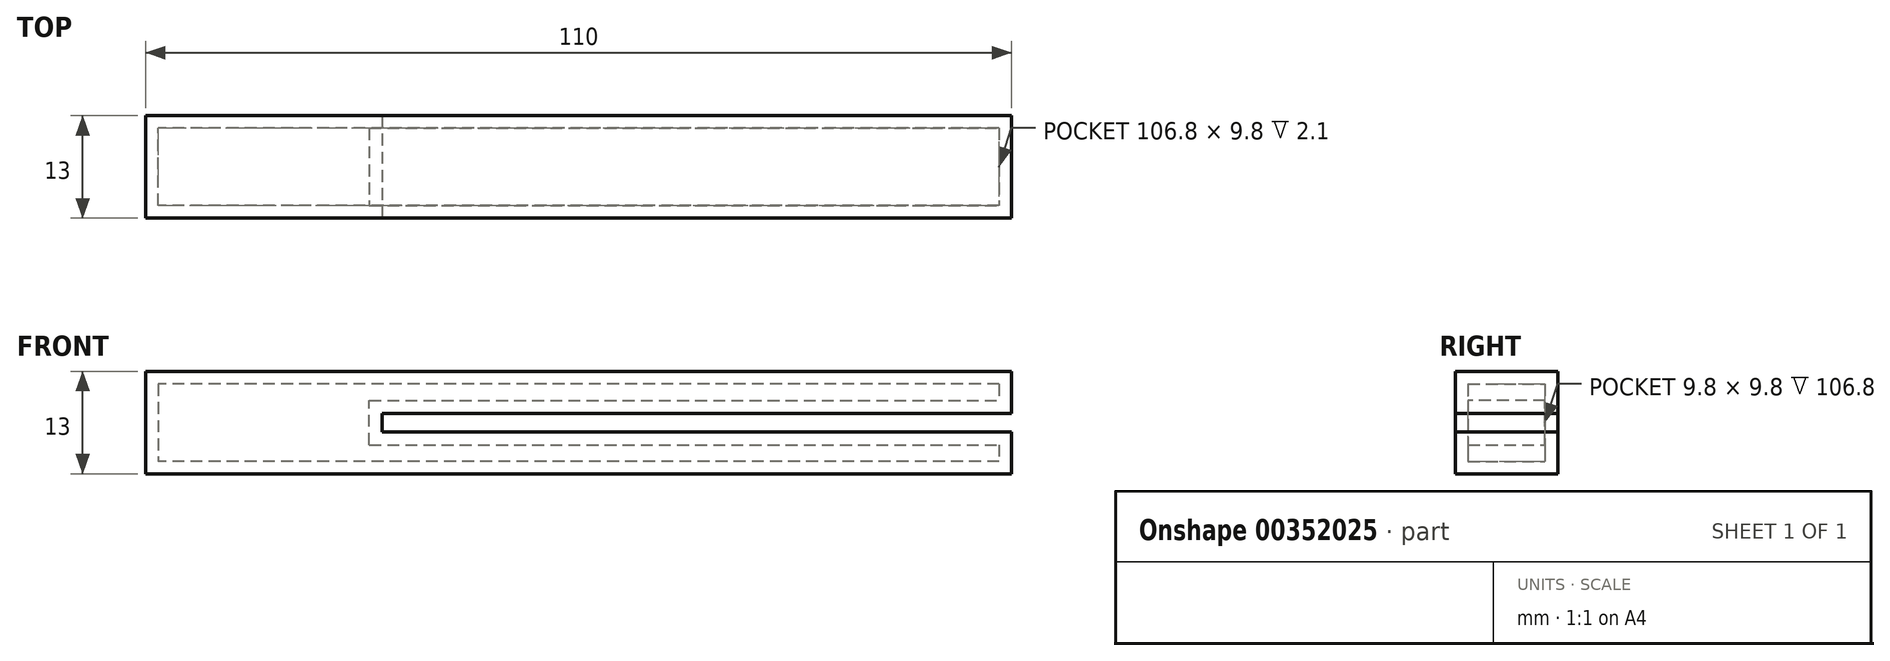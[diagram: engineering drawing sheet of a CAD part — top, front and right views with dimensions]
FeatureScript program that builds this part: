
annotation { "Feature Type Name" : "Feature", "Feature Type Description" : "" }
export const myFeature = defineFeature(function(context is Context, id is Id, definition is map)
    precondition{}
    {
        {
            var Q0;
            Q0=qCreatedBy(makeId("Right.planeOp"),FACE);
            var sketch = newSketch(context, id + "F0", { "sketchPlane" : qUnion([Q0])});
            skLineSegment(sketch, "E0.bottom", {"start": v(-6.5, 6.5) * mm, "end": v(6.5, 6.5) * mm});
            skLineSegment(sketch, "E0.top", {"start": v(-6.5, -6.5) * mm, "end": v(6.5, -6.5) * mm});
            skLineSegment(sketch, "E0.left", {"start": v(-6.5, 6.5) * mm, "end": v(-6.5, -6.5) * mm});
            skLineSegment(sketch, "E0.right", {"start": v(6.5, 6.5) * mm, "end": v(6.5, -6.5) * mm});
            skSolve(sketch);
        }
        {
            var Q0;
            Q0=qSketchRegion(id+"F0",true);
            extrude(context, id + "F1", {"entities" : qUnion([Q0]), "depth" : 110 * mm});
        }
        {
            var Q0;
            Q0=qCreatedBy(makeId("Right.planeOp"),FACE);
            cPlane(context, id + "F2", {"entities" : qUnion([Q0]), "cplaneType" : CPlaneType.OFFSET, "offset" : 110 * mm, "width" : 150 * mm, "height" : 150 * mm});
        }
        {
            var Q0;
            Q0=qCreatedBy(id+"F2.planeOp",FACE);
            var sketch = newSketch(context, id + "F3", { "sketchPlane" : qUnion([Q0])});
            skLineSegment(sketch, "E1", {"start": v(-6.5, 1.2) * mm, "end": v(-6.5, -1.2) * mm});
            skLineSegment(sketch, "E2", {"start": v(-6.5, -1.2) * mm, "end": v(6.5, -1.2) * mm});
            skLineSegment(sketch, "E3", {"start": v(6.5, -1.2) * mm, "end": v(6.5, 1.2) * mm});
            skLineSegment(sketch, "E4", {"start": v(6.5, 1.2) * mm, "end": v(-6.5, 1.2) * mm});
            skSolve(sketch);
        }
        {
            var Q0;
            Q0=makeQuery(id+"F3.imprint","IMPRINT",FACE,{"disambiguationData":[TD([[makeQuery(id+"F3.imprint","IMPRINT",EDGE,{"derivedFrom":sQuery(id+"F3.wireOp",EDGE,"E1")}),1.0]])]});
            extrude(context, id + "F4", {"entities" : qUnion([Q0]), "operationType" : NewBodyOperationType.REMOVE, "oppositeDirection" : true, "depth" : 80 * mm});
        }
        {
            var Q0;
            Q0=makeQuery(id+"F1.opExtrude","SWEPT_FACE",FACE,{"disambiguationData":[OSD([sQuery(id+"F0.wireOp",EDGE,"E0.left")])]});
            var Q1;
            Q1=makeQuery(id+"F1.opExtrude","SWEPT_BODY",BODY,{"disambiguationData":[OSD([sQuery(id+"F0.wireOp",EDGE,"E0.bottom"),sQuery(id+"F0.wireOp",EDGE,"E0.top"),sQuery(id+"F0.wireOp",EDGE,"E0.left"),sQuery(id+"F0.wireOp",EDGE,"E0.right")])]});
            shell(context, id + "F5", {"isHollow" : true, "entities" : qUnion([Q0]), "parts" : qUnion([Q1]), "thickness" : 1.6 * mm});
        }
    });
